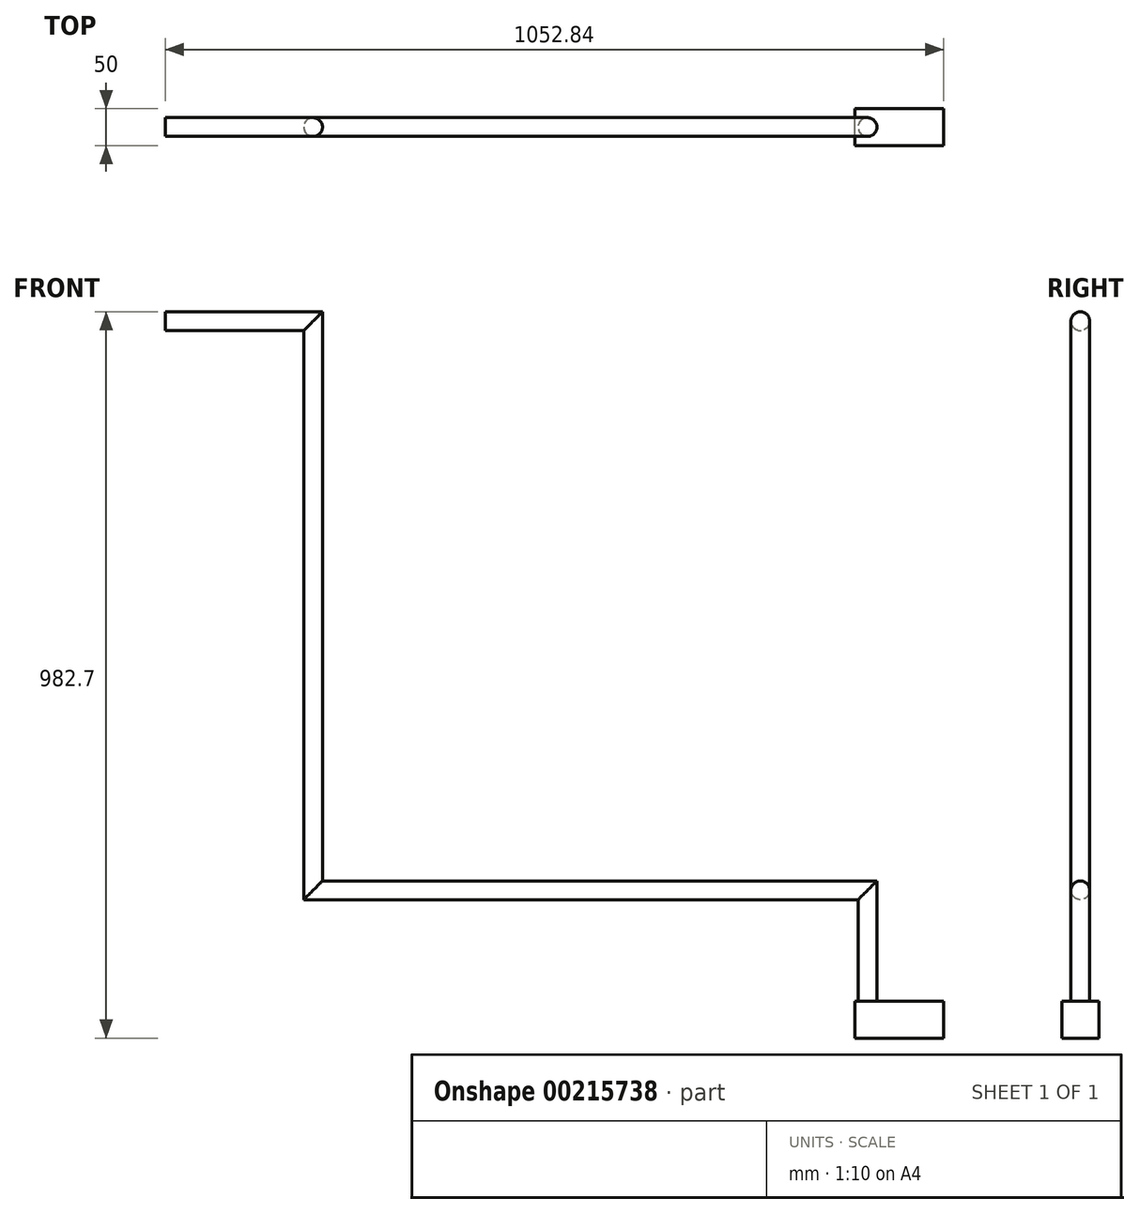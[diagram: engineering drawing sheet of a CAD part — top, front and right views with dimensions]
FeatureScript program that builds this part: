
annotation { "Feature Type Name" : "Feature", "Feature Type Description" : "" }
export const myFeature = defineFeature(function(context is Context, id is Id, definition is map)
    precondition{}
    {
        {
            var Q0;
            Q0=qCreatedBy(makeId("Front.planeOp"),FACE);
            var sketch = newSketch(context, id + "F0", { "sketchPlane" : qUnion([Q0])});
            skLineSegment(sketch, "E0.bottom", {"start": v(-17.16, 0) * mm, "end": v(102.84, 0) * mm});
            skLineSegment(sketch, "E0.top", {"start": v(-17.16, -50) * mm, "end": v(102.84, -50) * mm});
            skLineSegment(sketch, "E0.left", {"start": v(-17.16, 0) * mm, "end": v(-17.16, -50) * mm});
            skLineSegment(sketch, "E0.right", {"start": v(102.84, 0) * mm, "end": v(102.84, -50) * mm});
            skSolve(sketch);
        }
        {
            var Q0;
            Q0 = qSketchRegion(id + "F0", true);
            extrude(context, id + "F1", {"entities" : qUnion([Q0]), "depth" : 25 * mm, "hasSecondDirection" : true, "secondDirectionOppositeDirection" : true, "secondDirectionDepth" : 25 * mm});
        }
        {
            var Q0;
            Q0=qCreatedBy(makeId("Front.planeOp"),FACE);
            var sketch = newSketch(context, id + "F2", { "sketchPlane" : qUnion([Q0])});
            skLineSegment(sketch, "E1", {"start": v(0, 0) * mm, "end": v(0, 150) * mm});
            skLineSegment(sketch, "E2", {"start": v(0, 150) * mm, "end": v(-750, 150) * mm});
            skLineSegment(sketch, "E3", {"start": v(-750, 150) * mm, "end": v(-750, 920) * mm});
            skLineSegment(sketch, "E4", {"start": v(-750, 920) * mm, "end": v(-950, 920) * mm});
            skSolve(sketch);
        }
        {
            var Q0;
            Q0=qCreatedBy(makeId("Top.planeOp"),FACE);
            var sketch = newSketch(context, id + "F3", { "sketchPlane" : qUnion([Q0])});
            skCircle(sketch, "E5", {"center": v(0, 0) * mm, "radius": 12.7 * mm});
            skSolve(sketch);
        }
        {
            var Q0;
            Q0=makeQuery(id+"F3.imprint","IMPRINT",FACE,{"disambiguationData":[TD([[makeQuery(id+"F3.imprint","IMPRINT",EDGE,{"derivedFrom":sQuery(id+"F3.wireOp",EDGE,"E5")}),1.0]])]});
            var Q1;
            Q1=sQuery(id+"F2.wireOp",EDGE,"E2");
            var Q2;
            Q2=sQuery(id+"F2.wireOp",EDGE,"E1");
            var Q3;
            Q3=sQuery(id+"F2.wireOp",EDGE,"E3");
            var Q4;
            Q4=sQuery(id+"F2.wireOp",EDGE,"E4");
            sweep(context, id + "F4", {"operationType" : NewBodyOperationType.ADD, "profiles" : qUnion([Q0]), "path" : qUnion([Q1, Q2, Q3, Q4])});
        }
    });
